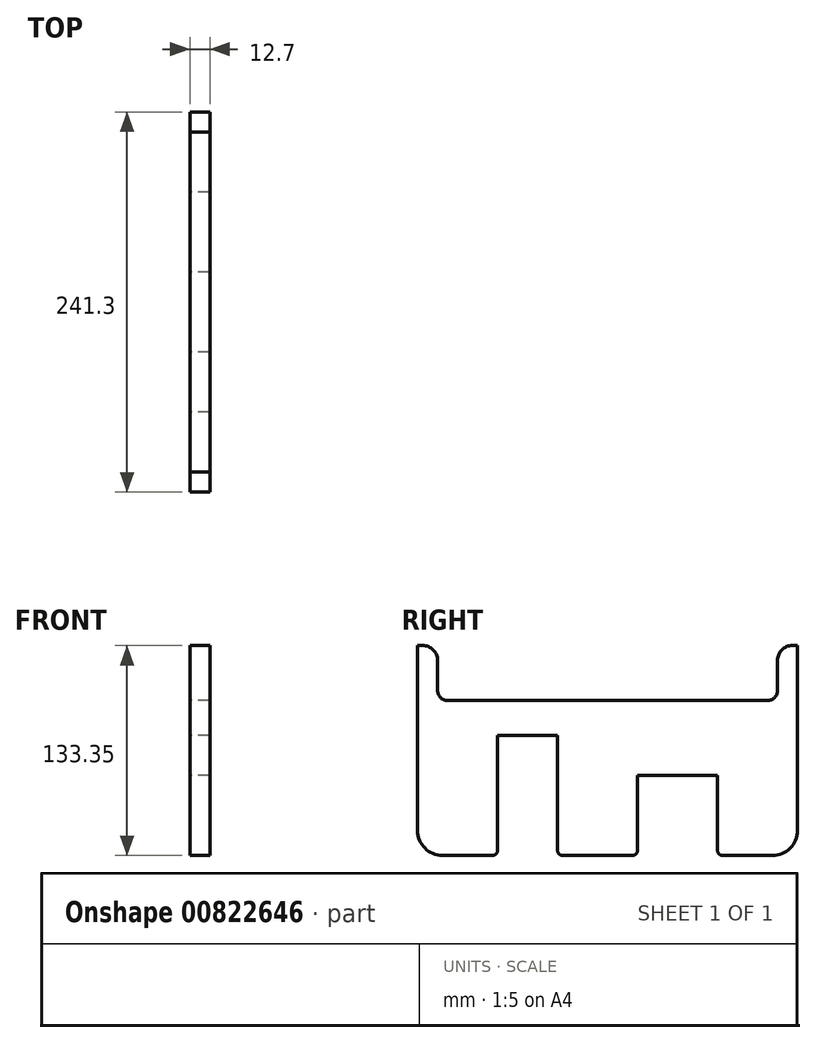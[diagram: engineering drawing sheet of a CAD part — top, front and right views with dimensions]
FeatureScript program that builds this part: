
annotation { "Feature Type Name" : "Feature", "Feature Type Description" : "" }
export const myFeature = defineFeature(function(context is Context, id is Id, definition is map)
    precondition{}
    {
        {
            var Q0;
            Q0=qCreatedBy(makeId("Right.planeOp"),FACE);
            var sketch = newSketch(context, id + "F0", { "sketchPlane" : qUnion([Q0])});
            skLineSegment(sketch, "E0", {"start": v(-86.45, 0) * mm, "end": v(-35.65, 0) * mm});
            skLineSegment(sketch, "E1", {"start": v(-35.65, 0) * mm, "end": v(-35.65, 76.2) * mm});
            skLineSegment(sketch, "E2", {"start": v(-35.65, 76.2) * mm, "end": v(2.45, 76.2) * mm});
            skLineSegment(sketch, "E3", {"start": v(2.45, 76.2) * mm, "end": v(2.45, 0) * mm});
            skLineSegment(sketch, "E4", {"start": v(2.45, 0) * mm, "end": v(53.25, 0) * mm});
            skLineSegment(sketch, "E5", {"start": v(53.25, 0) * mm, "end": v(53.25, 50.8) * mm});
            skLineSegment(sketch, "E6", {"start": v(53.25, 50.8) * mm, "end": v(104.05, 50.8) * mm});
            skLineSegment(sketch, "E7", {"start": v(104.05, 50.8) * mm, "end": v(104.05, 0) * mm});
            skLineSegment(sketch, "E8", {"start": v(104.05, 0) * mm, "end": v(154.85, 0) * mm});
            skLineSegment(sketch, "E9", {"start": v(154.85, 0) * mm, "end": v(154.85, 133.35) * mm});
            skLineSegment(sketch, "E10", {"start": v(154.85, 133.35) * mm, "end": v(142.15, 133.35) * mm});
            skLineSegment(sketch, "E11", {"start": v(142.15, 133.35) * mm, "end": v(142.15, 98.43) * mm});
            skLineSegment(sketch, "E12", {"start": v(142.15, 98.43) * mm, "end": v(-73.75, 98.42) * mm});
            skLineSegment(sketch, "E13", {"start": v(-73.75, 98.42) * mm, "end": v(-73.75, 133.35) * mm});
            skLineSegment(sketch, "E14", {"start": v(-73.75, 133.35) * mm, "end": v(-86.45, 133.35) * mm});
            skLineSegment(sketch, "E15", {"start": v(-86.45, 133.35) * mm, "end": v(-86.45, 0) * mm});
            skSolve(sketch);
        }
        {
            var Q0;
            Q0 = qSketchRegion(id + "F0", true);
            extrude(context, id + "F1", {"entities" : qUnion([Q0]), "endBound" : BoundingType.SYMMETRIC, "depth" : 12.7 * mm, "offsetDistance" : 25.4 * mm});
        }
        {
            var Q0;
            Q0=makeQuery(id+"F1.opExtrude","SWEPT_EDGE",EDGE,{"disambiguationData":[OSD([sQuery(id+"F0.wireOp",EDGE,"E4"),sQuery(id+"F0.wireOp",EDGE,"E5")])]});
            var Q1;
            Q1=makeQuery(id+"F1.opExtrude","SWEPT_EDGE",EDGE,{"disambiguationData":[OSD([sQuery(id+"F0.wireOp",EDGE,"E7"),sQuery(id+"F0.wireOp",EDGE,"E8")])]});
            var Q2;
            Q2=makeQuery(id+"F1.opExtrude","SWEPT_EDGE",EDGE,{"disambiguationData":[OSD([sQuery(id+"F0.wireOp",EDGE,"E3"),sQuery(id+"F0.wireOp",EDGE,"E4")])]});
            var Q3;
            Q3=makeQuery(id+"F1.opExtrude","SWEPT_EDGE",EDGE,{"disambiguationData":[OSD([sQuery(id+"F0.wireOp",EDGE,"E0"),sQuery(id+"F0.wireOp",EDGE,"E1")])]});
            fillet(context, id + "F2", {"entities" : qUnion([Q0, Q1, Q2, Q3]), "radius" : 3.17 * mm, "tangentPropagation" : true, "allowEdgeOverflow" : false});
        }
        {
            var Q0;
            Q0=makeQuery(id+"F1.opExtrude","SWEPT_EDGE",EDGE,{"disambiguationData":[OSD([sQuery(id+"F0.wireOp",EDGE,"E12"),sQuery(id+"F0.wireOp",EDGE,"E13")])]});
            var Q1;
            Q1=makeQuery(id+"F1.opExtrude","SWEPT_EDGE",EDGE,{"disambiguationData":[OSD([sQuery(id+"F0.wireOp",EDGE,"E11"),sQuery(id+"F0.wireOp",EDGE,"E12")])]});
            fillet(context, id + "F3", {"entities" : qUnion([Q0, Q1]), "radius" : 6.35 * mm, "tangentPropagation" : true, "allowEdgeOverflow" : false});
        }
        {
            var Q0;
            Q0=makeQuery(id+"F1.opExtrude","SWEPT_EDGE",EDGE,{"disambiguationData":[OSD([sQuery(id+"F0.wireOp",EDGE,"E13"),sQuery(id+"F0.wireOp",EDGE,"E14")])]});
            var Q1;
            Q1=makeQuery(id+"F1.opExtrude","SWEPT_EDGE",EDGE,{"disambiguationData":[OSD([sQuery(id+"F0.wireOp",EDGE,"E10"),sQuery(id+"F0.wireOp",EDGE,"E11")])]});
            fillet(context, id + "F4", {"entities" : qUnion([Q0, Q1]), "radius" : 9.52 * mm, "tangentPropagation" : true, "allowEdgeOverflow" : false});
        }
        {
            var Q0;
            Q0=makeQuery(id+"F1.opExtrude","SWEPT_EDGE",EDGE,{"disambiguationData":[OSD([sQuery(id+"F0.wireOp",EDGE,"E0"),sQuery(id+"F0.wireOp",EDGE,"E15")])]});
            var Q1;
            Q1=makeQuery(id+"F1.opExtrude","SWEPT_EDGE",EDGE,{"disambiguationData":[OSD([sQuery(id+"F0.wireOp",EDGE,"E8"),sQuery(id+"F0.wireOp",EDGE,"E9")])]});
            fillet(context, id + "F5", {"entities" : qUnion([Q0, Q1]), "radius" : 15.88 * mm, "tangentPropagation" : true, "allowEdgeOverflow" : false});
        }
    });
